# Revit family: Specialty_Equipment-Metal_Raceway-Hubbell_Wiring-Switch_Cover-HBL3040CE
name_source: partatom
category: Specialty Equipment
revit_build: Autodesk Revit 2015 (Build: 20140606_1530(x64)
units: mm (PartAtom-declared; Revit-internal decimal feet)

## types (2) — shared parameters
A = 4.50"
Assembly Code = D5090900
B = 2.75"
Default Elevation = 48.00"
Description = Switch Cover
Host Note = Add in Section View; Host to Wall
Manufacturer = Hubbell Wiring Device Kellems
Product Documentation Link = http://www.hubbellcatalog.com
Product Page URL = http://ecatalog.hubbell-wiring.com
Product data url = https://bimobject.com
URL = http://www.hubbell-wiring.com

## per-type parameters (varying)
| type | Cable Tray Material |
| HBL3040CEIV | Metal-Hubbell-Ivory |
| HBL3040CEGY | Metal-Hubbell-Gray |

note: column(s) folded — value = type name in every type: Model

## geometry (parser evidence)
native form markers: Blend x4, Sweep x2
no freeform markers — native parametric forms only
